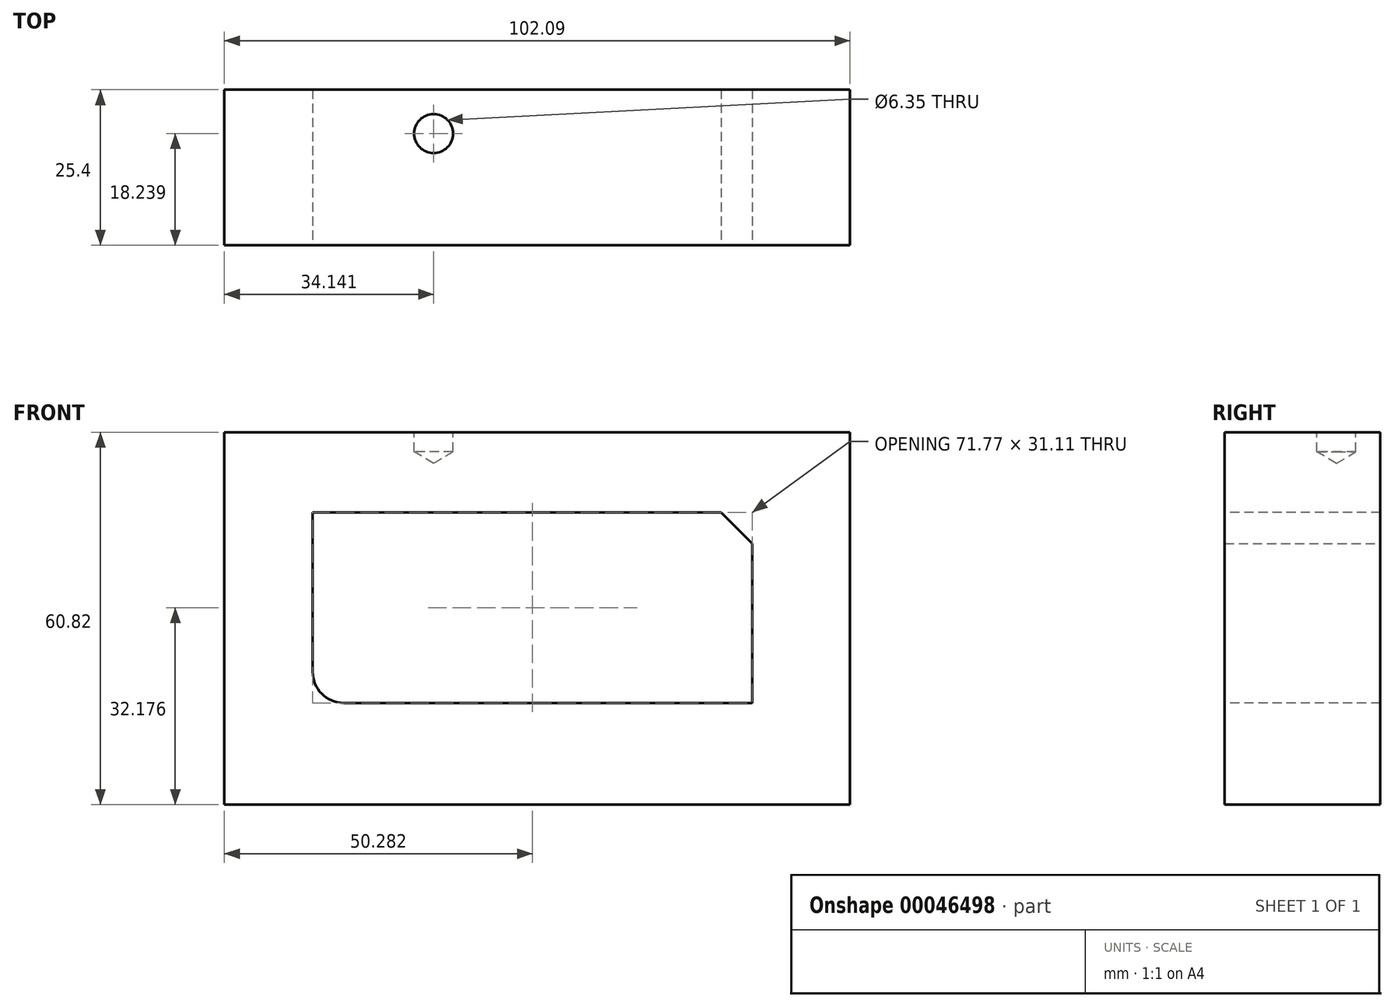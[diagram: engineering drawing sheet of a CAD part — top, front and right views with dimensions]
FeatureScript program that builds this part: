
annotation { "Feature Type Name" : "Feature", "Feature Type Description" : "" }
export const myFeature = defineFeature(function(context is Context, id is Id, definition is map)
    precondition{}
    {
        {
            var Q0;
            Q0=qCreatedBy(makeId("Front.planeOp"),FACE);
            var sketch = newSketch(context, id + "F0", { "sketchPlane" : qUnion([Q0])});
            skLineSegment(sketch, "E0.bottom", {"start": v(-64.62, 44.2) * mm, "end": v(37.47, 44.2) * mm});
            skLineSegment(sketch, "E0.top", {"start": v(-64.62, -16.62) * mm, "end": v(37.47, -16.62) * mm});
            skLineSegment(sketch, "E0.left", {"start": v(-64.62, 44.2) * mm, "end": v(-64.62, -16.62) * mm});
            skLineSegment(sketch, "E0.right", {"start": v(37.47, 44.2) * mm, "end": v(37.47, -16.62) * mm});
            skSolve(sketch);
        }
        {
            var Q0;
            Q0=makeQuery(id+"F0.imprint","IMPRINT",FACE,{"disambiguationData":[TD([[makeQuery(id+"F0.imprint","IMPRINT",EDGE,{"derivedFrom":sQuery(id+"F0.wireOp",EDGE,"E0.bottom")}),-1.0]])]});
            extrude(context, id + "F1", {"entities" : qUnion([Q0]), "depth" : 25.4 * mm});
        }
        {
            var Q0;
            Q0=makeQuery(id+"F1.opExtrude","CAP_FACE",FACE,{"disambiguationData":[OSD([sQuery(id+"F0.wireOp",EDGE,"E0.bottom"),sQuery(id+"F0.wireOp",EDGE,"E0.top"),sQuery(id+"F0.wireOp",EDGE,"E0.left"),sQuery(id+"F0.wireOp",EDGE,"E0.right")])],"isStart":false});
            var sketch = newSketch(context, id + "F2", { "sketchPlane" : qUnion([Q0])});
            skLineSegment(sketch, "E1.bottom", {"start": v(-50.22, 31.11) * mm, "end": v(21.55, 31.11) * mm});
            skLineSegment(sketch, "E1.top", {"start": v(-50.22, 0) * mm, "end": v(21.55, 0) * mm});
            skLineSegment(sketch, "E1.left", {"start": v(-50.22, 31.11) * mm, "end": v(-50.22, 0) * mm});
            skLineSegment(sketch, "E1.right", {"start": v(21.55, 31.11) * mm, "end": v(21.55, 0) * mm});
            skSolve(sketch);
        }
        {
            var Q0;
            Q0=makeQuery(id+"F2.imprint","IMPRINT",FACE,{"disambiguationData":[TD([[makeQuery(id+"F2.imprint","IMPRINT",EDGE,{"derivedFrom":sQuery(id+"F2.wireOp",EDGE,"E1.bottom")}),-1.0]])]});
            extrude(context, id + "F3", {"entities" : qUnion([Q0]), "operationType" : NewBodyOperationType.REMOVE, "endBound" : BoundingType.THROUGH_ALL, "oppositeDirection" : true, "depth" : 25.4 * mm});
        }
        {
            var Q0;
            Q0=makeQuery(id+"F3.boolean.opBoolean","COPY",EDGE,{"derivedFrom":makeQuery(id+"F3.opExtrude","SWEPT_EDGE",EDGE,{"disambiguationData":[OSD([sQuery(id+"F2.wireOp",EDGE,"E1.top"),sQuery(id+"F2.wireOp",EDGE,"E1.left")])]})});
            fillet(context, id + "F4", {"entities" : qUnion([Q0]), "radius" : 5.08 * mm, "tangentPropagation" : true, "allowEdgeOverflow" : false});
        }
        {
            var Q0;
            Q0=makeQuery(id+"F3.boolean.opBoolean","COPY",EDGE,{"derivedFrom":makeQuery(id+"F3.opExtrude","SWEPT_EDGE",EDGE,{"disambiguationData":[OSD([sQuery(id+"F2.wireOp",EDGE,"E1.bottom"),sQuery(id+"F2.wireOp",EDGE,"E1.right")])]})});
            chamfer(context, id + "F5", {"entities" : qUnion([Q0]), "width" : 5.08 * mm, "tangentPropagation" : true});
        }
        {
            var Q0;
            Q0=makeQuery(id+"F1.opExtrude","SWEPT_FACE",FACE,{"disambiguationData":[OSD([sQuery(id+"F0.wireOp",EDGE,"E0.bottom")])]});
            var sketch = newSketch(context, id + "F6", { "sketchPlane" : qUnion([Q0])});
            skCircle(sketch, "E2", {"center": v(-30.48, -7.16) * mm, "radius": 4.4 * mm});
            skSolve(sketch);
        }
        {
            var Q0;
            Q0=sQuery(id+"F6.wireOp",VERTEX,"E2.center");
            var Q1;
            Q1=makeQuery(id+"F1.opExtrude","SWEPT_BODY",BODY,{"disambiguationData":[OSD([sQuery(id+"F0.wireOp",EDGE,"E0.bottom"),sQuery(id+"F0.wireOp",EDGE,"E0.top"),sQuery(id+"F0.wireOp",EDGE,"E0.left"),sQuery(id+"F0.wireOp",EDGE,"E0.right")])]});
            hole(context, id + "F7", {"style" : HoleStyle.SIMPLE, "holeDiameter" : 6.35 * mm, "endStyle" : HoleEndStyle.BLIND, "holeDepth" : 3.17 * mm, "locations" : qUnion([Q0]), "scope" : qUnion([Q1])});
        }
    });
